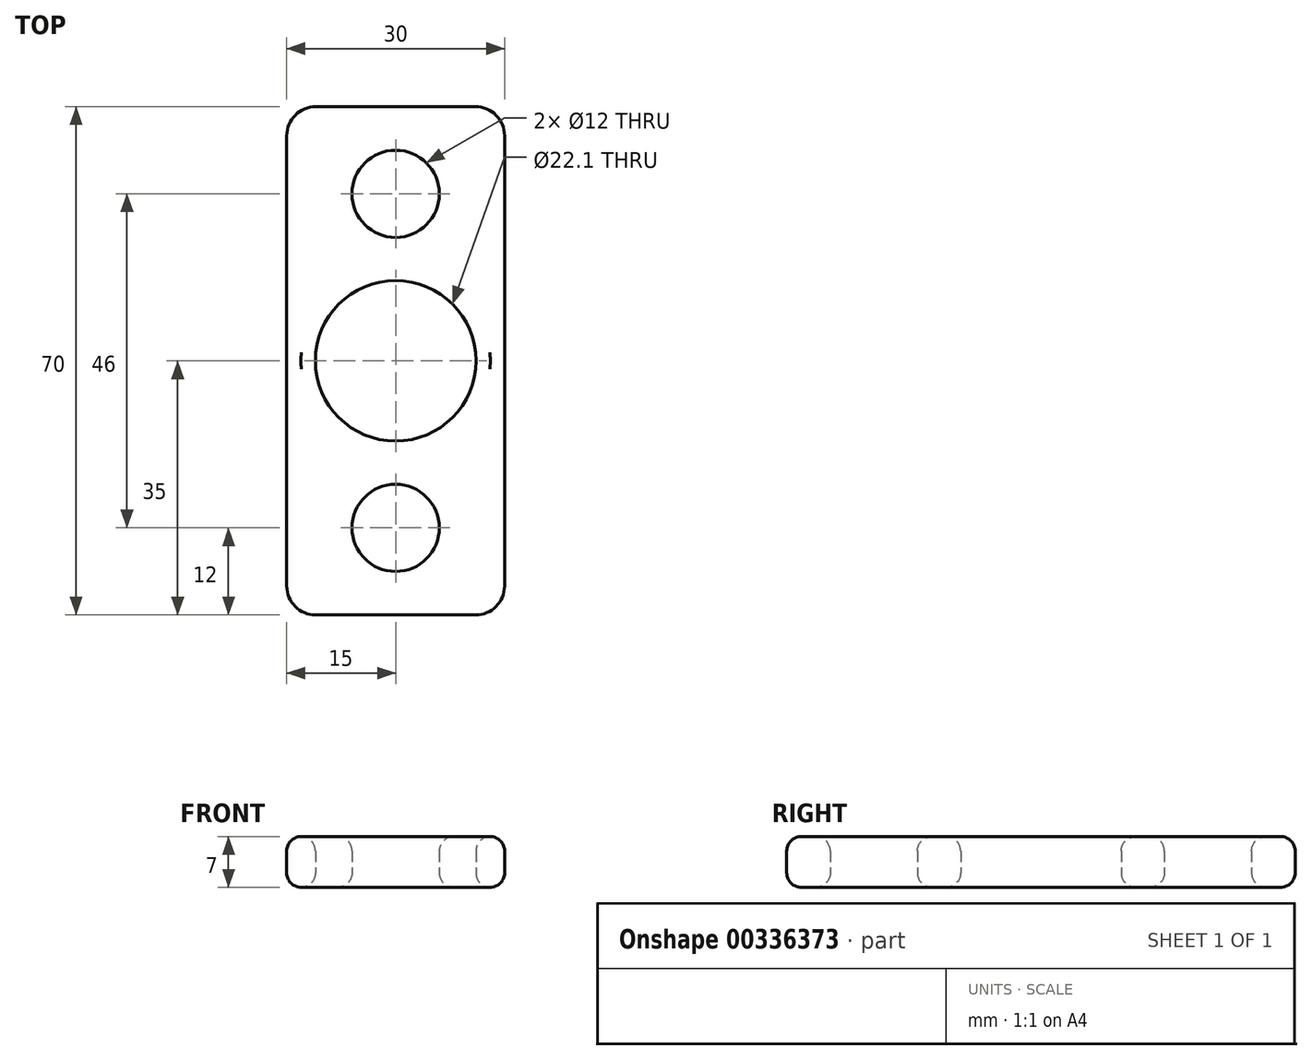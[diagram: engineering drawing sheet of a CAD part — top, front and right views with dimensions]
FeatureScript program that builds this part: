
annotation { "Feature Type Name" : "Feature", "Feature Type Description" : "" }
export const myFeature = defineFeature(function(context is Context, id is Id, definition is map)
    precondition{}
    {
        {
            var Q0;
            Q0=qCreatedBy(makeId("Top.planeOp"),FACE);
            var sketch = newSketch(context, id + "F0", { "sketchPlane" : qUnion([Q0])});
            skLineSegment(sketch, "E0.bottom", {"start": v(15, 35) * mm, "end": v(-15, 35) * mm});
            skLineSegment(sketch, "E0.top", {"start": v(15, -35) * mm, "end": v(-15, -35) * mm});
            skLineSegment(sketch, "E0.left", {"start": v(15, 35) * mm, "end": v(15, -35) * mm});
            skLineSegment(sketch, "E0.right", {"start": v(-15, 35) * mm, "end": v(-15, -35) * mm});
            skPoint(sketch, "E0.middle", {"position": v(0, 0) * mm});
            skCircle(sketch, "E1", {"center": v(0, 0) * mm, "radius": 11.05 * mm});
            skCircle(sketch, "E2", {"center": v(0, 23) * mm, "radius": 6 * mm});
            skCircle(sketch, "E3.MirrorC", {"center": v(0, -23) * mm, "radius": 6 * mm});
            skSolve(sketch);
        }
        {
            var Q0;
            Q0=makeQuery(id+"F0.imprint","IMPRINT",FACE,{"disambiguationData":[TD([[makeQuery(id+"F0.imprint","IMPRINT",EDGE,{"derivedFrom":sQuery(id+"F0.wireOp",EDGE,"E0.bottom")}),1.0]])]});
            extrude(context, id + "F1", {"entities" : qUnion([Q0]), "depth" : 7 * mm, "offsetDistance" : 25 * mm});
        }
        {
            var Q0;
            Q0=makeQuery(id+"F1.opExtrude","CAP_FACE",FACE,{"disambiguationData":[OSD([sQuery(id+"F0.wireOp",EDGE,"E0.bottom"),sQuery(id+"F0.wireOp",EDGE,"E0.top"),sQuery(id+"F0.wireOp",EDGE,"E0.left"),sQuery(id+"F0.wireOp",EDGE,"E0.right"),sQuery(id+"F0.wireOp",EDGE,"E1"),sQuery(id+"F0.wireOp",EDGE,"E2"),sQuery(id+"F0.wireOp",EDGE,"E3.MirrorC")])],"isStart":false});
            var Q1;
            Q1=makeQuery(id+"F1.opExtrude","CAP_FACE",FACE,{"disambiguationData":[OSD([sQuery(id+"F0.wireOp",EDGE,"E0.bottom"),sQuery(id+"F0.wireOp",EDGE,"E0.top"),sQuery(id+"F0.wireOp",EDGE,"E0.left"),sQuery(id+"F0.wireOp",EDGE,"E0.right"),sQuery(id+"F0.wireOp",EDGE,"E1"),sQuery(id+"F0.wireOp",EDGE,"E2"),sQuery(id+"F0.wireOp",EDGE,"E3.MirrorC")])],"isStart":true});
            fillet(context, id + "F2", {"entities" : qUnion([Q0, Q1]), "tangentPropagation" : true, "radius" : 2 * mm, "defaultsChanged" : false, "vertexSettings" : [], "allowEdgeOverflow" : false});
        }
        {
            var Q0;
            Q0=makeQuery(id+"F1.opExtrude","SWEPT_EDGE",EDGE,{"disambiguationData":[OSD([sQuery(id+"F0.wireOp",EDGE,"E0.top"),sQuery(id+"F0.wireOp",EDGE,"E0.right")])]});
            var Q1;
            Q1=makeQuery(id+"F1.opExtrude","SWEPT_EDGE",EDGE,{"disambiguationData":[OSD([sQuery(id+"F0.wireOp",EDGE,"E0.top"),sQuery(id+"F0.wireOp",EDGE,"E0.left")])]});
            var Q2;
            Q2=makeQuery(id+"F1.opExtrude","SWEPT_EDGE",EDGE,{"disambiguationData":[OSD([sQuery(id+"F0.wireOp",EDGE,"E0.bottom"),sQuery(id+"F0.wireOp",EDGE,"E0.left")])]});
            var Q3;
            Q3=makeQuery(id+"F1.opExtrude","SWEPT_EDGE",EDGE,{"disambiguationData":[OSD([sQuery(id+"F0.wireOp",EDGE,"E0.bottom"),sQuery(id+"F0.wireOp",EDGE,"E0.right")])]});
            fillet(context, id + "F3", {"entities" : qUnion([Q0, Q1, Q2, Q3]), "tangentPropagation" : true, "radius" : 4 * mm, "defaultsChanged" : false, "vertexSettings" : [], "allowEdgeOverflow" : false});
        }
    });
